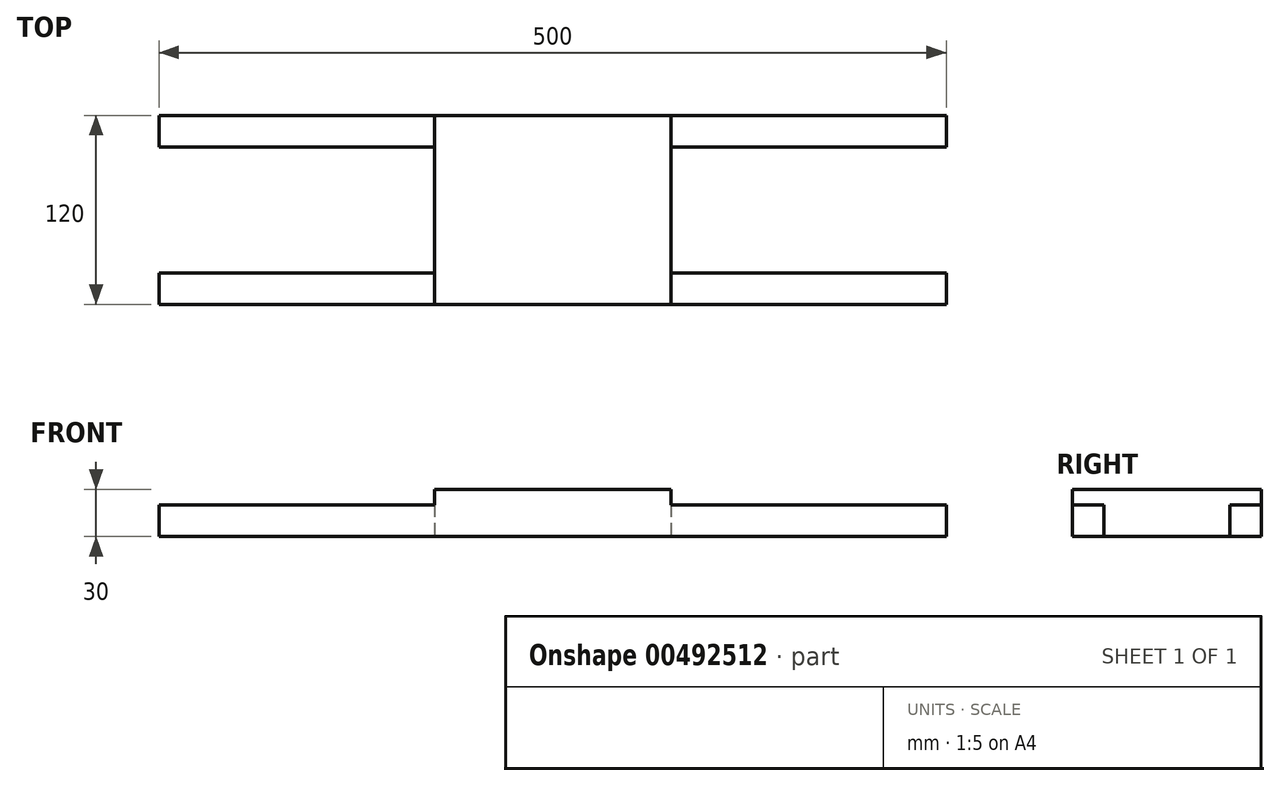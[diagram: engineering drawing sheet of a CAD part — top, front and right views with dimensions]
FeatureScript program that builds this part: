
annotation { "Feature Type Name" : "Feature", "Feature Type Description" : "" }
export const myFeature = defineFeature(function(context is Context, id is Id, definition is map)
    precondition{}
    {
        {
            var Q0;
            Q0=qCreatedBy(makeId("Top.planeOp"),FACE);
            var sketch = newSketch(context, id + "F0", { "sketchPlane" : qUnion([Q0])});
            skLineSegment(sketch, "E0.bottom", {"start": v(-250, -60) * mm, "end": v(250, -60) * mm});
            skLineSegment(sketch, "E0.top", {"start": v(-250, 60) * mm, "end": v(250, 60) * mm});
            skLineSegment(sketch, "E0.left", {"start": v(-250, -60) * mm, "end": v(-250, 60) * mm});
            skLineSegment(sketch, "E0.right", {"start": v(250, -60) * mm, "end": v(250, 60) * mm});
            skPoint(sketch, "E0.middle", {"position": v(0, 0) * mm});
            skLineSegment(sketch, "E1.bottom", {"start": v(-250, -40) * mm, "end": v(250, -40) * mm});
            skLineSegment(sketch, "E1.top", {"start": v(-250, 40) * mm, "end": v(250, 40) * mm});
            skLineSegment(sketch, "E2.bottom", {"start": v(75, -60) * mm, "end": v(-75, -60) * mm});
            skLineSegment(sketch, "E2.top", {"start": v(75, 60) * mm, "end": v(-75, 60) * mm});
            skLineSegment(sketch, "E2.left", {"start": v(75, -60) * mm, "end": v(75, 60) * mm});
            skLineSegment(sketch, "E2.right", {"start": v(-75, -60) * mm, "end": v(-75, 60) * mm});
            skSolve(sketch);
        }
        {
            var Q0;
            {var subQ0=sQuery(id+"F0.wireOp",EDGE,"E0.top");Q0=makeQuery(id+"F0.imprint","IMPRINT",FACE,{"disambiguationData":[TD([[makeQuery(id+"F0.imprint","IMPRINT",EDGE,{"derivedFrom":subQ0}),-1.0]])]});}
            var Q1;
            {var subQ0=sQuery(id+"F0.wireOp",EDGE,"E0.bottom");Q1=makeQuery(id+"F0.imprint","IMPRINT",FACE,{"disambiguationData":[TD([[makeQuery(id+"F0.imprint","IMPRINT",EDGE,{"derivedFrom":subQ0}),1.0]])]});}
            var Q2;
            {var subQ0=sQuery(id+"F0.wireOp",EDGE,"E2.right");var subQ1=sQuery(id+"F0.wireOp",EDGE,"E1.bottom");var subQ2=makeQuery(id+"F0.imprint","INTERSECT",VERTEX,{"derivedFrom":[subQ1,subQ0]});Q2=makeQuery(id+"F0.imprint","IMPRINT",FACE,{"disambiguationData":[TD([[makeQuery(id+"F0.imprint","IMPRINT",EDGE,{"disambiguationData":[TD([[subQ2,-1.0]])],"derivedFrom":subQ1}),1.0]])]});}
            var Q3;
            {var subQ5=sQuery(id+"F0.wireOp",EDGE,"E2.bottom");Q3=makeQuery(id+"F0.imprint","IMPRINT",FACE,{"disambiguationData":[TD([[makeQuery(id+"F0.imprint","IMPRINT",EDGE,{"derivedFrom":subQ5}),-1.0]])]});}
            var Q4;
            {var subQ5=sQuery(id+"F0.wireOp",EDGE,"E2.top");Q4=makeQuery(id+"F0.imprint","IMPRINT",FACE,{"disambiguationData":[TD([[makeQuery(id+"F0.imprint","IMPRINT",EDGE,{"derivedFrom":subQ5}),1.0]])]});}
            extrude(context, id + "F1", {"entities" : qUnion([Q0, Q1, Q2, Q3, Q4]), "depth" : 20 * mm});
        }
        {
            var Q0;
            Q0=makeQuery(id+"F1.opExtrude","CAP_FACE",FACE,{"disambiguationData":[OSD([sQuery(id+"F0.wireOp",EDGE,"E0.bottom"),sQuery(id+"F0.wireOp",EDGE,"E0.top"),sQuery(id+"F0.wireOp",EDGE,"E0.left"),sQuery(id+"F0.wireOp",EDGE,"E0.right"),sQuery(id+"F0.wireOp",EDGE,"E1.bottom"),sQuery(id+"F0.wireOp",EDGE,"E1.top"),sQuery(id+"F0.wireOp",EDGE,"E2.bottom"),sQuery(id+"F0.wireOp",EDGE,"E2.top"),sQuery(id+"F0.wireOp",EDGE,"E2.left"),sQuery(id+"F0.wireOp",EDGE,"E2.right")])],"isStart":false});
            var sketch = newSketch(context, id + "F2", { "sketchPlane" : qUnion([Q0])});
            skLineSegment(sketch, "E3.bottom", {"start": v(-75, 40) * mm, "end": v(75, 40) * mm});
            skLineSegment(sketch, "E3.top", {"start": v(-75, -40) * mm, "end": v(75, -40) * mm});
            skLineSegment(sketch, "E3.left", {"start": v(-75, 40) * mm, "end": v(-75, -40) * mm});
            skLineSegment(sketch, "E3.right", {"start": v(75, 40) * mm, "end": v(75, -40) * mm});
            skLineSegment(sketch, "E4", {"start": v(-75, 40) * mm, "end": v(-75, 60) * mm});
            skLineSegment(sketch, "E5", {"start": v(-75, 60) * mm, "end": v(75, 60) * mm});
            skLineSegment(sketch, "E6", {"start": v(75, 60) * mm, "end": v(75, -60) * mm});
            skLineSegment(sketch, "E7", {"start": v(75, -60) * mm, "end": v(-79.46, -60) * mm});
            skLineSegment(sketch, "E8", {"start": v(-75, -40) * mm, "end": v(-75, -60) * mm});
            skSolve(sketch);
        }
        {
            var Q0;
            {var subQ0=sQuery(id+"F2.wireOp",EDGE,"E3.bottom");Q0=makeQuery(id+"F2.imprint","IMPRINT",FACE,{"disambiguationData":[TD([[makeQuery(id+"F2.imprint","IMPRINT",EDGE,{"derivedFrom":subQ0}),-1.0]])]});}
            var Q1;
            {var subQ0=sQuery(id+"F2.wireOp",EDGE,"E3.bottom");Q1=makeQuery(id+"F2.imprint","IMPRINT",FACE,{"disambiguationData":[TD([[makeQuery(id+"F2.imprint","IMPRINT",EDGE,{"derivedFrom":subQ0}),1.0]])]});}
            var Q2;
            {var subQ0=sQuery(id+"F2.wireOp",EDGE,"E3.top");Q2=makeQuery(id+"F2.imprint","IMPRINT",FACE,{"disambiguationData":[TD([[makeQuery(id+"F2.imprint","IMPRINT",EDGE,{"derivedFrom":subQ0}),-1.0]])]});}
            extrude(context, id + "F3", {"entities" : qUnion([Q0, Q1, Q2]), "operationType" : NewBodyOperationType.ADD, "depth" : 10 * mm});
        }
    });
